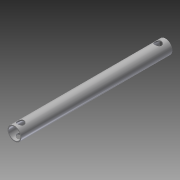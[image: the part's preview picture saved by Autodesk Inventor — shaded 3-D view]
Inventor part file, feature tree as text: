
AUTODESK INVENTOR PART (.ipt)
format: ipt  version: 2013 (Build 170138000, 138)  size: 97,792 bytes
history: native  units: in
note: dims shown in document units (in); Inventor stores cm internally (conversion verified against a paired STEP export)
features: extrude x2, plane x2, sketch x2
ambient origin geometry x8: Origin, YZ Plane, XZ Plane, XY Plane, X Axis, Y Axis, Z Axis, Center Point
bodies: Solid1 (feature_tree)
feature tree (6):
  extrude  "Extrusion1"  Depth=0.85in
  plane  "Work Plane2"
  extrude  "Extrusion2"  Depth=0.5in TaperAngle=90.0deg
  sketch  "Sketch1"  dims[d0=1.0in d1=0.85in]
  plane  "Work Plane1"
  sketch  "Sketch2"  dims[d2=11.0in d3=0.0in d4=90.0deg d5=0.5in d6=11.0in d7=0.45in d8=0.5in d9=0.55in d10=0.5in d11=11.0in d12=0.0in]
